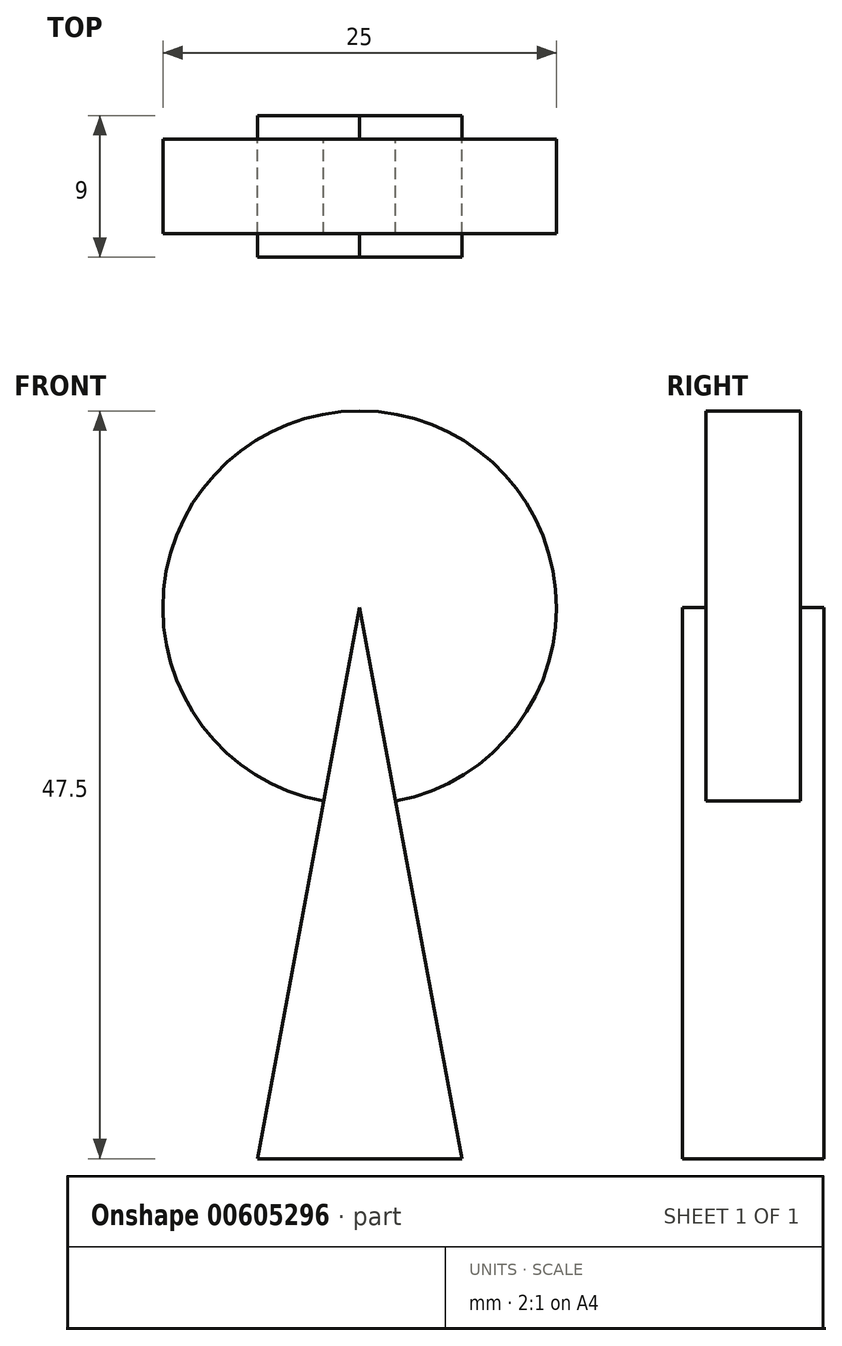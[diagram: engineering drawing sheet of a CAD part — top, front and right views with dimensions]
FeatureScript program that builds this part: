
annotation { "Feature Type Name" : "Feature", "Feature Type Description" : "" }
export const myFeature = defineFeature(function(context is Context, id is Id, definition is map)
    precondition{}
    {
        {
            var Q0;
            Q0=qCreatedBy(makeId("Front.planeOp"),FACE);
            var sketch = newSketch(context, id + "F0", { "sketchPlane" : qUnion([Q0])});
            skCircle(sketch, "E0", {"center": v(0, 37.5) * mm, "radius": 12.5 * mm});
            skLineSegment(sketch, "E1", {"start": v(0, 50) * mm, "end": v(0, 0) * mm});
            skSolve(sketch);
        }
        {
            var Q0;
            {var subQ0=sQuery(id+"F0.wireOp",EDGE,"E1");var subQ1=sQuery(id+"F0.wireOp",EDGE,"E0");var subQ2=makeQuery(id+"F0.imprint","INTERSECT",VERTEX,{"disambiguationData":[OD(0.0)],"derivedFrom":[subQ1,subQ0]});Q0=makeQuery(id+"F0.imprint","IMPRINT",FACE,{"disambiguationData":[TD([[makeQuery(id+"F0.imprint","IMPRINT",EDGE,{"disambiguationData":[TD([[subQ2,1.0]])],"derivedFrom":subQ1}),1.0]])]});}
            var Q1;
            {var subQ0=sQuery(id+"F0.wireOp",EDGE,"E1");var subQ1=sQuery(id+"F0.wireOp",EDGE,"E0");var subQ2=makeQuery(id+"F0.imprint","INTERSECT",VERTEX,{"disambiguationData":[OD(0.0)],"derivedFrom":[subQ1,subQ0]});Q1=makeQuery(id+"F0.imprint","IMPRINT",FACE,{"disambiguationData":[TD([[makeQuery(id+"F0.imprint","IMPRINT",EDGE,{"disambiguationData":[TD([[subQ2,-1.0]])],"derivedFrom":subQ1}),1.0]])]});}
            extrude(context, id + "F1", {"entities" : qUnion([Q0, Q1]), "endBound" : BoundingType.SYMMETRIC, "depth" : 6 * mm, "offsetDistance" : 25.4 * mm});
        }
        {
            var Q0;
            Q0=qCreatedBy(makeId("Front.planeOp"),FACE);
            var sketch = newSketch(context, id + "F2", { "sketchPlane" : qUnion([Q0])});
            skLineSegment(sketch, "E2", {"start": v(0, 37.5) * mm, "end": v(-6.5, 2.5) * mm});
            skLineSegment(sketch, "E3", {"start": v(-6.5, 2.5) * mm, "end": v(6.5, 2.5) * mm});
            skLineSegment(sketch, "E4", {"start": v(6.5, 2.5) * mm, "end": v(0, 37.5) * mm});
            skSolve(sketch);
        }
        {
            var Q0;
            Q0 = qSketchRegion(id + "F2", true);
            extrude(context, id + "F3", {"entities" : qUnion([Q0]), "operationType" : NewBodyOperationType.ADD, "endBound" : BoundingType.SYMMETRIC, "depth" : 9 * mm, "offsetDistance" : 25 * mm});
        }
        {
            var Q0;
            Q0=makeQuery(id+"F1.opExtrude","SWEPT_BODY",BODY,{"disambiguationData":[OSD([sQuery(id+"F0.wireOp",EDGE,"E0")])]});
            var Q1;
            Q1=qCreatedBy(makeId("Front.planeOp"),FACE);
            mirror(context, id + "F4", {"operationType" : NewBodyOperationType.ADD, "entities" : qUnion([Q0]), "mirrorPlane" : qUnion([Q1])});
        }
    });
